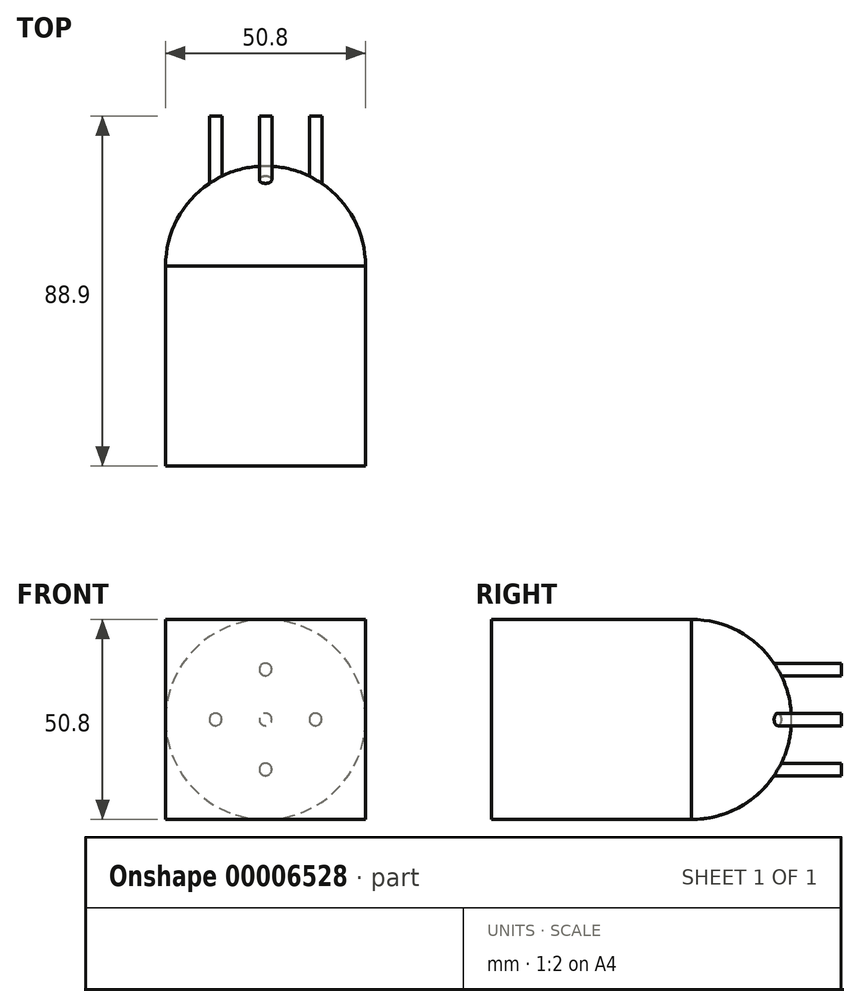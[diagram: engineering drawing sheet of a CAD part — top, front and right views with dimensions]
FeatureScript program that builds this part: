
annotation { "Feature Type Name" : "Feature", "Feature Type Description" : "" }
export const myFeature = defineFeature(function(context is Context, id is Id, definition is map)
    precondition{}
    {
        {
            var Q0;
            Q0=qCreatedBy(makeId("Top.planeOp"),FACE);
            var sketch = newSketch(context, id + "F0", { "sketchPlane" : qUnion([Q0])});
            skLineSegment(sketch, "E0.bottom", {"start": v(0, 0) * mm, "end": v(50.8, 0) * mm});
            skLineSegment(sketch, "E0.top", {"start": v(0, -50.8) * mm, "end": v(50.8, -50.8) * mm});
            skLineSegment(sketch, "E0.left", {"start": v(0, 0) * mm, "end": v(0, -50.8) * mm});
            skLineSegment(sketch, "E0.right", {"start": v(50.8, 0) * mm, "end": v(50.8, -50.8) * mm});
            skSolve(sketch);
        }
        {
            var Q0;
            Q0=makeQuery(id+"F0.imprint","IMPRINT",FACE,{"disambiguationData":[TD([[makeQuery(id+"F0.imprint","IMPRINT",EDGE,{"derivedFrom":sQuery(id+"F0.wireOp",EDGE,"E0.bottom")}),-1.0]])]});
            extrude(context, id + "F1", {"entities" : qUnion([Q0]), "endBound" : BoundingType.SYMMETRIC, "depth" : 50.8 * mm});
        }
        {
            var Q0;
            Q0=qCreatedBy(makeId("Top.planeOp"),FACE);
            var sketch = newSketch(context, id + "F2", { "sketchPlane" : qUnion([Q0])});
            skArc(sketch, "E1", {"start": v(25.4, 25.4) * mm, "mid": v(7.44, 17.96) * mm, "end": v(0, 0) * mm});
            skLineSegment(sketch, "E2", {"start": v(0, 0) * mm, "end": v(25.4, 0) * mm});
            skLineSegment(sketch, "E3", {"start": v(25.4, 0) * mm, "end": v(25.4, 25.4) * mm});
            skSolve(sketch);
        }
        {
            var Q0;
            Q0=makeQuery(id+"F2.imprint","IMPRINT",FACE,{"disambiguationData":[TD([[makeQuery(id+"F2.imprint","IMPRINT",EDGE,{"derivedFrom":sQuery(id+"F2.wireOp",EDGE,"E1")}),1.0]])]});
            var Q1;
            Q1=sQuery(id+"F2.wireOp",EDGE,"E3");
            revolve(context, id + "F3", {"operationType" : NewBodyOperationType.ADD, "entities" : qUnion([Q0]), "axis" : qUnion([Q1]), "revolveType" : RevolveType.FULL});
        }
        {
            var Q0;
            Q0=makeQuery(id+"F1.opExtrude","SWEPT_FACE",FACE,{"disambiguationData":[OSD([sQuery(id+"F0.wireOp",EDGE,"E0.top")])]});
            var sketch = newSketch(context, id + "F4", { "sketchPlane" : qUnion([Q0])});
            skCircle(sketch, "E4", {"center": v(25.4, 0) * mm, "radius": 1.59 * mm});
            skLineSegment(sketch, "E5", {"start": v(25.4, 25.4) * mm, "end": v(25.4, -25.4) * mm, "construction": true});
            skLineSegment(sketch, "E6", {"start": v(0, 0) * mm, "end": v(50.8, 0) * mm, "construction": true});
            skCircle(sketch, "E7", {"center": v(25.4, 12.7) * mm, "radius": 1.59 * mm});
            skCircle(sketch, "E8.1.0", {"center": v(12.7, 0) * mm, "radius": 1.59 * mm});
            skCircle(sketch, "E8.2.0", {"center": v(25.4, -12.7) * mm, "radius": 1.59 * mm});
            skCircle(sketch, "E8.3.0", {"center": v(38.1, 0) * mm, "radius": 1.59 * mm});
            skSolve(sketch);
        }
        {
            var Q0;
            {Q0=qUnion([makeQuery(id+"F4.imprint","IMPRINT",FACE,{"disambiguationData":[TD([[makeQuery(id+"F4.imprint","IMPRINT",EDGE,{"derivedFrom":sQuery(id+"F4.wireOp",EDGE,"E4")}),1.0]])]}),makeQuery(id+"F4.imprint","IMPRINT",FACE,{"disambiguationData":[TD([[makeQuery(id+"F4.imprint","IMPRINT",EDGE,{"derivedFrom":sQuery(id+"F4.wireOp",EDGE,"E7")}),1.0]])]}),makeQuery(id+"F4.imprint","IMPRINT",FACE,{"disambiguationData":[TD([[makeQuery(id+"F4.imprint","IMPRINT",EDGE,{"derivedFrom":sQuery(id+"F4.wireOp",EDGE,"E8.1.0")}),1.0]])]}),makeQuery(id+"F4.imprint","IMPRINT",FACE,{"disambiguationData":[TD([[makeQuery(id+"F4.imprint","IMPRINT",EDGE,{"derivedFrom":sQuery(id+"F4.wireOp",EDGE,"E8.2.0")}),1.0]])]}),makeQuery(id+"F4.imprint","IMPRINT",FACE,{"disambiguationData":[TD([[makeQuery(id+"F4.imprint","IMPRINT",EDGE,{"derivedFrom":sQuery(id+"F4.wireOp",EDGE,"E8.3.0")}),1.0]])]})]);}
            extrude(context, id + "F5", {"entities" : qUnion([Q0]), "operationType" : NewBodyOperationType.ADD, "oppositeDirection" : true, "depth" : 88.9 * mm});
        }
    });
